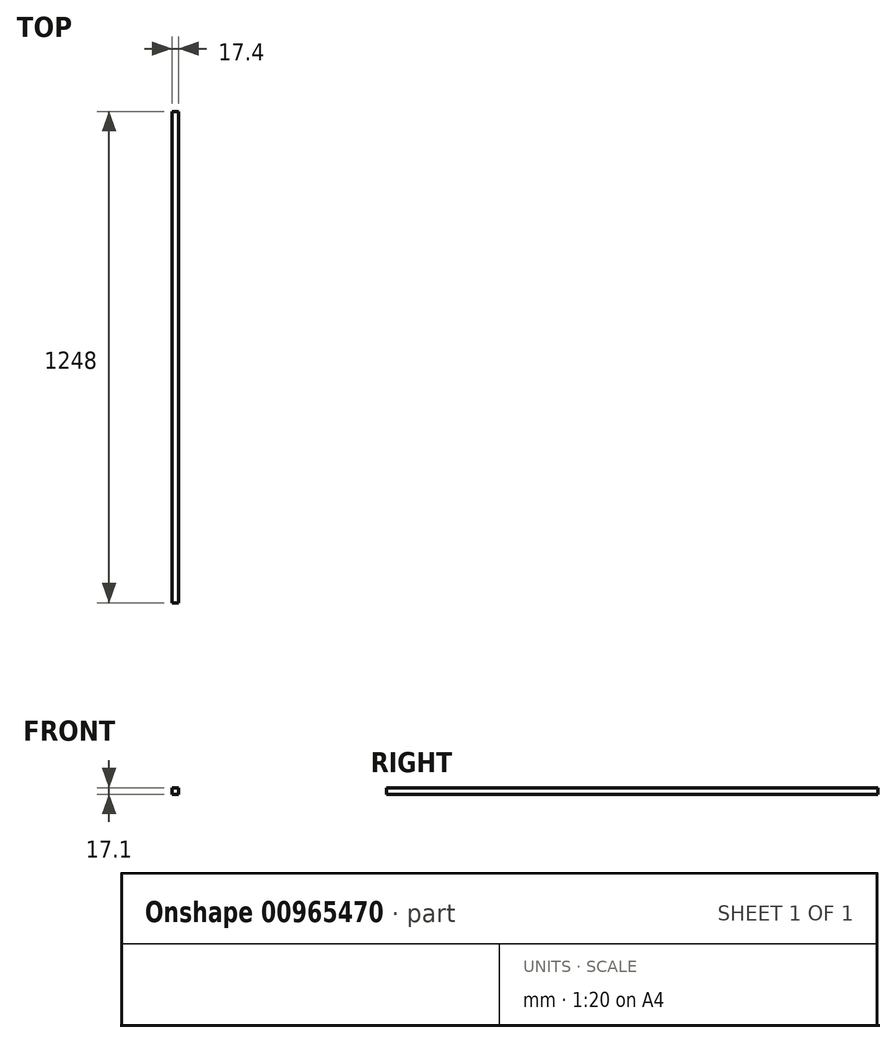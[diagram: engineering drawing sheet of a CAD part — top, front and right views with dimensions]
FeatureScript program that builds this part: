
annotation { "Feature Type Name" : "Feature", "Feature Type Description" : "" }
export const myFeature = defineFeature(function(context is Context, id is Id, definition is map)
    precondition{}
    {
        {
            var Q0;
            Q0=qCreatedBy(makeId("Front.planeOp"),FACE);
            var sketch = newSketch(context, id + "F0", { "sketchPlane" : qUnion([Q0])});
            skLineSegment(sketch, "E0.bottom", {"start": v(-8.7, -8.55) * mm, "end": v(8.7, -8.55) * mm});
            skLineSegment(sketch, "E0.top", {"start": v(-8.7, 8.55) * mm, "end": v(8.7, 8.55) * mm});
            skLineSegment(sketch, "E0.left", {"start": v(-8.7, -8.55) * mm, "end": v(-8.7, 8.55) * mm});
            skLineSegment(sketch, "E0.right", {"start": v(8.7, -8.55) * mm, "end": v(8.7, 8.55) * mm});
            skPoint(sketch, "E0.middle", {"position": v(0, 0) * mm});
            skSolve(sketch);
        }
        {
            var Q0;
            Q0=makeQuery(id+"F0.imprint","IMPRINT",FACE,{"disambiguationData":[TD([[makeQuery(id+"F0.imprint","IMPRINT",EDGE,{"derivedFrom":sQuery(id+"F0.wireOp",EDGE,"E0.bottom")}),1.0]])]});
            extrude(context, id + "F1", {"entities" : qUnion([Q0]), "depth" : 1248 * mm, "offsetDistance" : 25.4 * mm});
        }
    });
